# Revit family: LAMP_SUSPENSION DOBLE 962749X
name_source: partatom
category: Modelos genéricos
revit_build: Autodesk Revit LT 2015 (Build: 20140606_1530(x64)
units: mm (PartAtom-declared; Revit-internal decimal feet)

## types (2) — shared parameters
Accessory type = Suspension
Comentarios de tipo = Availability of switching between accessories through visibility parameters when placed in a project.
Fabricante = LAMP LIGHTING
Installation instructions = http://admin.lamp.es
Last update = 23/02/2018
Manufacturer URL = http://www.lamp.es
Manufacturer country = Spain
Manufacturer name = LAMP LIGHTING
Material Cables = LAMP_Acero genérico
Maximun length (mm) = 3000 mm  [stored 9.84252 ft]
Model explanation = Availability of switching between accessories through visibility parameters when placed in a project.
Product URL = http://www.lamp.es
Product datasheet = http://admin.lamp.es
Weight = 0.63 kg

## per-type parameters (varying)
| type | Descripción | Finish | Material Carcasa | Modelo | Product code |
| WHITE | ACC. DB ELECMEC SUSP WH. | White | LAMP_Plástico genérico BL | 9627490 | 9627490 |
| GREY | ACC. DB ELECMEC SUSP GR. | Grey | LAMP_Plástico genérico GR | 9627493 | 9627493 |

note: [stored X ft] marks values corroborated as IEEE doubles in the binary element streams (Revit-internal decimal feet)
